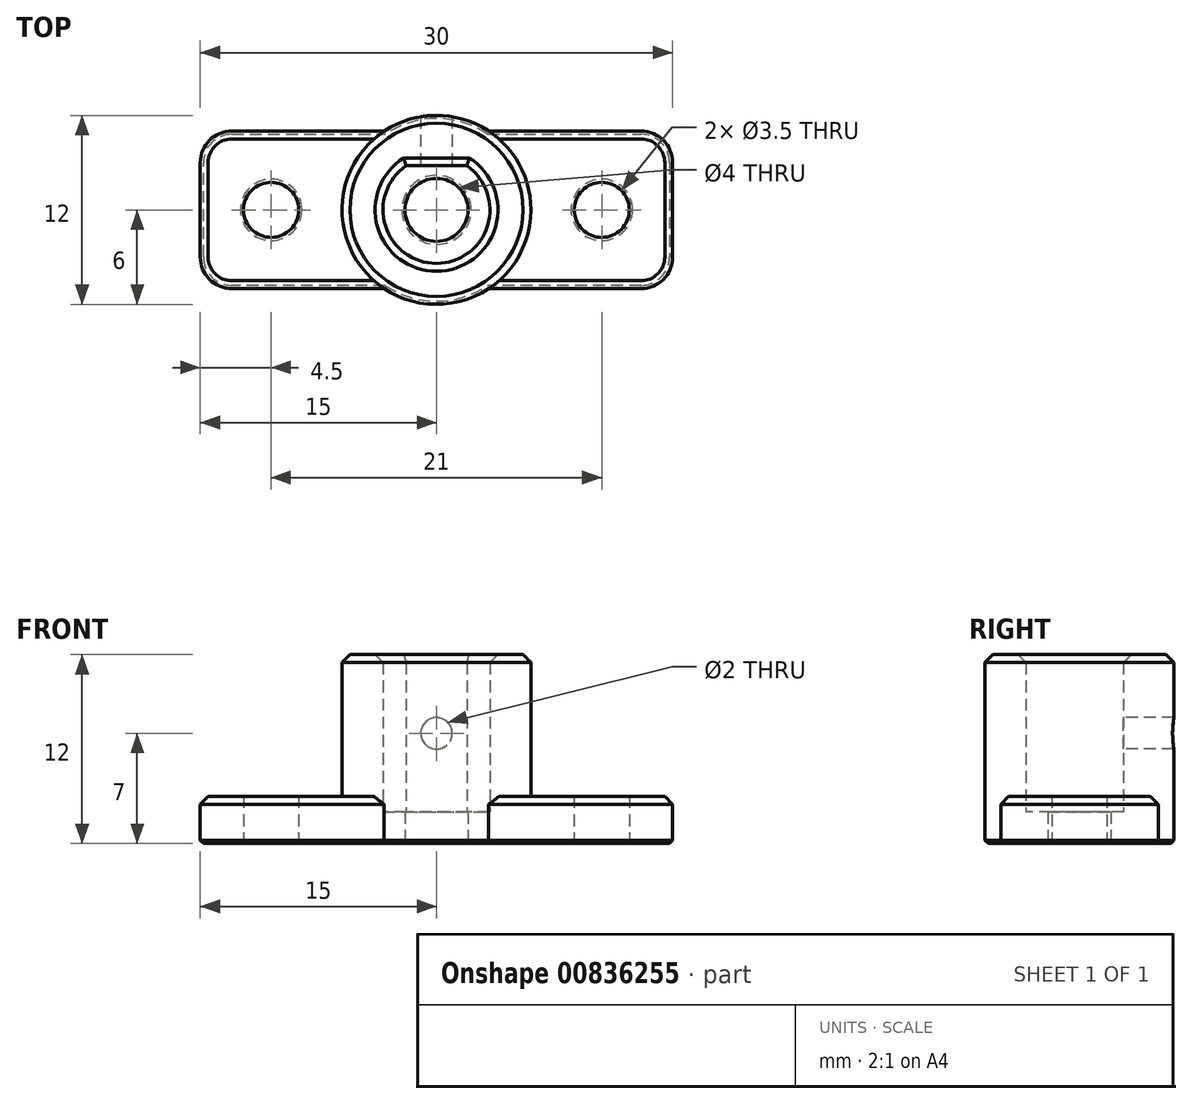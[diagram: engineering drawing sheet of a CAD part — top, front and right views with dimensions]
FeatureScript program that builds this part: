
annotation { "Feature Type Name" : "Feature", "Feature Type Description" : "" }
export const myFeature = defineFeature(function(context is Context, id is Id, definition is map)
    precondition{}
    {
        {
            var Q0;
            Q0=qCreatedBy(makeId("Top.planeOp"),FACE);
            var sketch = newSketch(context, id + "F0", { "sketchPlane" : qUnion([Q0])});
            skArc(sketch, "E0", {"start": v(-1.8, 2.4) * mm, "mid": v(0, -3) * mm, "end": v(1.8, 2.4) * mm, "construction": true});
            skCircle(sketch, "E1", {"center": v(0, 0) * mm, "radius": 6 * mm});
            skLineSegment(sketch, "E2", {"start": v(0, -3) * mm, "end": v(0, 2.4) * mm, "construction": true});
            skLineSegment(sketch, "E3", {"start": v(0, 2.4) * mm, "end": v(1.8, 2.4) * mm, "construction": true});
            skLineSegment(sketch, "E4", {"start": v(0, 2.4) * mm, "end": v(-1.8, 2.4) * mm, "construction": true});
            skLineSegment(sketch, "E5.0", {"start": v(0, 2.8) * mm, "end": v(-1.93, 2.8) * mm});
            skLineSegment(sketch, "E5.1", {"start": v(0, 2.8) * mm, "end": v(1.93, 2.8) * mm});
            skArc(sketch, "E5.2", {"start": v(-1.93, 2.8) * mm, "mid": v(0, -3.4) * mm, "end": v(1.93, 2.8) * mm});
            skLineSegment(sketch, "E6.bottom", {"start": v(13, -5) * mm, "end": v(-13, -5) * mm});
            skLineSegment(sketch, "E6.top", {"start": v(13, 5) * mm, "end": v(-13, 5) * mm});
            skLineSegment(sketch, "E6.left", {"start": v(15, -3) * mm, "end": v(15, 3) * mm});
            skLineSegment(sketch, "E6.right", {"start": v(-15, -3) * mm, "end": v(-15, 3) * mm});
            skLineSegment(sketch, "E7", {"start": v(6, 0) * mm, "end": v(15, 0) * mm, "construction": true});
            skCircle(sketch, "E8", {"center": v(10.5, 0) * mm, "radius": 1.75 * mm});
            skCircle(sketch, "E9.MirrorC", {"center": v(-10.5, 0) * mm, "radius": 1.75 * mm});
            skPoint(sketch, "E10.visualSharp", {"position": v(-15, 5) * mm});
            skArc(sketch, "E10.filletArc", {"start": v(-13, 5) * mm, "mid": v(-14.41, 4.41) * mm, "end": v(-15, 3) * mm});
            skPoint(sketch, "E11.visualSharp", {"position": v(-15, -5) * mm});
            skArc(sketch, "E11.filletArc", {"start": v(-15, -3) * mm, "mid": v(-14.41, -4.41) * mm, "end": v(-13, -5) * mm});
            skPoint(sketch, "E12.visualSharp", {"position": v(15, -5) * mm});
            skArc(sketch, "E12.filletArc", {"start": v(13, -5) * mm, "mid": v(14.41, -4.41) * mm, "end": v(15, -3) * mm});
            skPoint(sketch, "E13.visualSharp", {"position": v(15, 5) * mm});
            skArc(sketch, "E13.filletArc", {"start": v(15, 3) * mm, "mid": v(14.41, 4.41) * mm, "end": v(13, 5) * mm});
            skCircle(sketch, "E14", {"center": v(0, 0) * mm, "radius": 2 * mm});
            skSolve(sketch);
        }
        {
            var Q0;
            Q0=makeQuery(id+"F0.imprint","IMPRINT",FACE,{"disambiguationData":[TD([[makeQuery(id+"F0.imprint","IMPRINT",EDGE,{"derivedFrom":sQuery(id+"F0.wireOp",EDGE,"E5.0")}),-1.0]])]});
            var Q1;
            {var subQ0=sQuery(id+"F0.wireOp",EDGE,"E6.top");var subQ1=sQuery(id+"F0.wireOp",EDGE,"E1");var subQ2=makeQuery(id+"F0.imprint","INTERSECT",VERTEX,{"disambiguationData":[OD(0.0)],"derivedFrom":[subQ1,subQ0]});Q1=makeQuery(id+"F0.imprint","IMPRINT",FACE,{"disambiguationData":[TD([[makeQuery(id+"F0.imprint","IMPRINT",EDGE,{"disambiguationData":[TD([[subQ2,1.0]])],"derivedFrom":subQ1}),1.0]])]});}
            var Q2;
            {var subQ0=sQuery(id+"F0.wireOp",EDGE,"E6.bottom");var subQ1=sQuery(id+"F0.wireOp",EDGE,"E1");var subQ2=makeQuery(id+"F0.imprint","INTERSECT",VERTEX,{"disambiguationData":[OD(0.0)],"derivedFrom":[subQ1,subQ0]});Q2=makeQuery(id+"F0.imprint","IMPRINT",FACE,{"disambiguationData":[TD([[makeQuery(id+"F0.imprint","IMPRINT",EDGE,{"disambiguationData":[TD([[subQ2,-1.0]])],"derivedFrom":subQ1}),1.0]])]});}
            extrude(context, id + "F1", {"entities" : qUnion([Q0, Q1, Q2]), "depth" : 12 * mm, "offsetDistance" : 25 * mm});
        }
        {
            var Q0;
            Q0=makeQuery(id+"F0.imprint","IMPRINT",FACE,{"disambiguationData":[TD([[makeQuery(id+"F0.imprint","IMPRINT",EDGE,{"derivedFrom":sQuery(id+"F0.wireOp",EDGE,"E6.left")}),1.0]])]});
            var Q1;
            Q1=makeQuery(id+"F0.imprint","IMPRINT",FACE,{"disambiguationData":[TD([[makeQuery(id+"F0.imprint","IMPRINT",EDGE,{"derivedFrom":sQuery(id+"F0.wireOp",EDGE,"E6.right")}),-1.0]])]});
            extrude(context, id + "F2", {"entities" : qUnion([Q0, Q1]), "operationType" : NewBodyOperationType.ADD, "depth" : 3 * mm, "offsetDistance" : 25 * mm});
        }
        {
            var Q0;
            Q0=makeQuery(id+"F0.imprint","IMPRINT",FACE,{"disambiguationData":[TD([[makeQuery(id+"F0.imprint","IMPRINT",EDGE,{"derivedFrom":sQuery(id+"F0.wireOp",EDGE,"E5.0")}),1.0]])]});
            extrude(context, id + "F3", {"entities" : qUnion([Q0]), "operationType" : NewBodyOperationType.ADD, "depth" : 2 * mm, "offsetDistance" : 25 * mm});
        }
        {
            var Q0;
            Q0=makeQuery(id+"F1.opExtrude","SWEPT_FACE",FACE,{"disambiguationData":[OSD([sQuery(id+"F0.wireOp",EDGE,"E5.0"),sQuery(id+"F0.wireOp",EDGE,"E5.1")])]});
            var sketch = newSketch(context, id + "F4", { "sketchPlane" : qUnion([Q0])});
            skLineSegment(sketch, "E15", {"start": v(-1.93, 12) * mm, "end": v(1.93, 2) * mm, "construction": true});
            skCircle(sketch, "E16", {"center": v(0, 7) * mm, "radius": 1 * mm});
            skSolve(sketch);
        }
        {
            var Q0;
            Q0=makeQuery(id+"F4.imprint","IMPRINT",FACE,{"disambiguationData":[TD([[makeQuery(id+"F4.imprint","IMPRINT",EDGE,{"derivedFrom":sQuery(id+"F4.wireOp",EDGE,"E16")}),1.0]])]});
            extrude(context, id + "F5", {"entities" : qUnion([Q0]), "operationType" : NewBodyOperationType.REMOVE, "oppositeDirection" : true, "depth" : 25 * mm, "offsetDistance" : 25 * mm});
        }
        {
            var Q0;
            {var subQ0=sQuery(id+"F0.wireOp",EDGE,"E6.bottom");Q0=makeQuery(id+"F2.opExtrude","CAP_EDGE",EDGE,{"disambiguationData":[OSD([subQ0]),TDD([makeQuery(id+"F0.imprint","IMPRINT",EDGE,{"disambiguationData":[TD([[makeQuery(id+"F0.imprint","INTERSECT",VERTEX,{"derivedFrom":[subQ0,sQuery(id+"F0.wireOp",EDGE,"E12.filletArc")]}),-1.0]])],"derivedFrom":subQ0})])],"isStart":false});}
            var Q1;
            Q1=makeQuery(id+"F2.opExtrude","CAP_EDGE",EDGE,{"disambiguationData":[OSD([sQuery(id+"F0.wireOp",EDGE,"E12.filletArc")])],"isStart":false});
            var Q2;
            Q2=makeQuery(id+"F2.opExtrude","CAP_EDGE",EDGE,{"disambiguationData":[OSD([sQuery(id+"F0.wireOp",EDGE,"E6.left")])],"isStart":false});
            var Q3;
            Q3=makeQuery(id+"F2.opExtrude","CAP_EDGE",EDGE,{"disambiguationData":[OSD([sQuery(id+"F0.wireOp",EDGE,"E13.filletArc")])],"isStart":false});
            var Q4;
            {var subQ0=sQuery(id+"F0.wireOp",EDGE,"E6.top");Q4=makeQuery(id+"F2.opExtrude","CAP_EDGE",EDGE,{"disambiguationData":[OSD([subQ0]),TDD([makeQuery(id+"F0.imprint","IMPRINT",EDGE,{"disambiguationData":[TD([[makeQuery(id+"F0.imprint","INTERSECT",VERTEX,{"derivedFrom":[subQ0,sQuery(id+"F0.wireOp",EDGE,"E13.filletArc")]}),-1.0]])],"derivedFrom":subQ0})])],"isStart":false});}
            var Q5;
            {var subQ0=sQuery(id+"F0.wireOp",EDGE,"E6.top");Q5=makeQuery(id+"F2.opExtrude","CAP_EDGE",EDGE,{"disambiguationData":[OSD([subQ0]),TDD([makeQuery(id+"F0.imprint","IMPRINT",EDGE,{"disambiguationData":[TD([[makeQuery(id+"F0.imprint","INTERSECT",VERTEX,{"derivedFrom":[subQ0,sQuery(id+"F0.wireOp",EDGE,"E10.filletArc")]}),1.0]])],"derivedFrom":subQ0})])],"isStart":false});}
            var Q6;
            Q6=makeQuery(id+"F2.opExtrude","CAP_EDGE",EDGE,{"disambiguationData":[OSD([sQuery(id+"F0.wireOp",EDGE,"E10.filletArc")])],"isStart":false});
            var Q7;
            Q7=makeQuery(id+"F2.opExtrude","CAP_EDGE",EDGE,{"disambiguationData":[OSD([sQuery(id+"F0.wireOp",EDGE,"E6.right")])],"isStart":false});
            var Q8;
            Q8=makeQuery(id+"F2.opExtrude","CAP_EDGE",EDGE,{"disambiguationData":[OSD([sQuery(id+"F0.wireOp",EDGE,"E11.filletArc")])],"isStart":false});
            var Q9;
            {var subQ0=sQuery(id+"F0.wireOp",EDGE,"E6.bottom");Q9=makeQuery(id+"F2.opExtrude","CAP_EDGE",EDGE,{"disambiguationData":[OSD([subQ0]),TDD([makeQuery(id+"F0.imprint","IMPRINT",EDGE,{"disambiguationData":[TD([[makeQuery(id+"F0.imprint","INTERSECT",VERTEX,{"derivedFrom":[subQ0,sQuery(id+"F0.wireOp",EDGE,"E11.filletArc")]}),1.0]])],"derivedFrom":subQ0})])],"isStart":false});}
            var Q10;
            Q10=makeQuery(id+"F1.opExtrude","CAP_EDGE",EDGE,{"disambiguationData":[OSD([sQuery(id+"F0.wireOp",EDGE,"E1")])],"isStart":false});
            var Q11;
            Q11=makeQuery(id+"F1.opExtrude","CAP_EDGE",EDGE,{"disambiguationData":[OSD([sQuery(id+"F0.wireOp",EDGE,"E5.2")])],"isStart":false});
            var Q12;
            Q12=makeQuery(id+"F1.opExtrude","CAP_EDGE",EDGE,{"disambiguationData":[OSD([sQuery(id+"F0.wireOp",EDGE,"E5.0"),sQuery(id+"F0.wireOp",EDGE,"E5.1")])],"isStart":false});
            chamfer(context, id + "F6", {"entities" : qUnion([Q0, Q1, Q2, Q3, Q4, Q5, Q6, Q7, Q8, Q9, Q10, Q11, Q12]), "width" : 0.5 * mm, "tangentPropagation" : true});
        }
        {
            var Q0;
            {var subQ0=sQuery(id+"F0.wireOp",EDGE,"E6.top");Q0=makeQuery(id+"F2.opExtrude","CAP_EDGE",EDGE,{"disambiguationData":[OSD([subQ0]),TDD([makeQuery(id+"F0.imprint","IMPRINT",EDGE,{"disambiguationData":[TD([[makeQuery(id+"F0.imprint","INTERSECT",VERTEX,{"derivedFrom":[subQ0,sQuery(id+"F0.wireOp",EDGE,"E13.filletArc")]}),-1.0]])],"derivedFrom":subQ0})])],"isStart":true});}
            var Q1;
            {var subQ1=sQuery(id+"F0.wireOp",EDGE,"E6.top");var subQ3=sQuery(id+"F0.wireOp",EDGE,"E1");var subQ4=sQuery(id+"F0.wireOp",EDGE,"E13.filletArc");Q1=makeQuery(id+"F2.boolean.opBoolean","SPLIT",EDGE,{"disambiguationData":[TD([makeQuery(id+"F2.opExtrude","SWEPT_FACE",FACE,{"disambiguationData":[OSD([subQ1]),TDD([makeQuery(id+"F0.imprint","IMPRINT",EDGE,{"disambiguationData":[TD([[makeQuery(id+"F0.imprint","INTERSECT",VERTEX,{"derivedFrom":[subQ1,subQ4]}),-1.0]])],"derivedFrom":subQ1})])]})])],"derivedFrom":makeQuery(id+"F1.opExtrude","CAP_EDGE",EDGE,{"disambiguationData":[OSD([subQ3])],"isStart":true})});}
            var Q2;
            {var subQ2=sQuery(id+"F0.wireOp",EDGE,"E6.bottom");var subQ3=sQuery(id+"F0.wireOp",EDGE,"E1");var subQ4=sQuery(id+"F0.wireOp",EDGE,"E12.filletArc");Q2=makeQuery(id+"F2.boolean.opBoolean","SPLIT",EDGE,{"disambiguationData":[TD([makeQuery(id+"F2.opExtrude","SWEPT_FACE",FACE,{"disambiguationData":[OSD([subQ2]),TDD([makeQuery(id+"F0.imprint","IMPRINT",EDGE,{"disambiguationData":[TD([[makeQuery(id+"F0.imprint","INTERSECT",VERTEX,{"derivedFrom":[subQ2,subQ4]}),-1.0]])],"derivedFrom":subQ2})])]})])],"derivedFrom":makeQuery(id+"F1.opExtrude","CAP_EDGE",EDGE,{"disambiguationData":[OSD([subQ3])],"isStart":true})});}
            var Q3;
            {var subQ0=sQuery(id+"F0.wireOp",EDGE,"E6.bottom");Q3=makeQuery(id+"F2.opExtrude","CAP_EDGE",EDGE,{"disambiguationData":[OSD([subQ0]),TDD([makeQuery(id+"F0.imprint","IMPRINT",EDGE,{"disambiguationData":[TD([[makeQuery(id+"F0.imprint","INTERSECT",VERTEX,{"derivedFrom":[subQ0,sQuery(id+"F0.wireOp",EDGE,"E11.filletArc")]}),1.0]])],"derivedFrom":subQ0})])],"isStart":true});}
            var Q4;
            Q4=makeQuery(id+"F2.opExtrude","CAP_EDGE",EDGE,{"disambiguationData":[OSD([sQuery(id+"F0.wireOp",EDGE,"E8")])],"isStart":true});
            var Q5;
            Q5=makeQuery(id+"F3.opExtrude","CAP_EDGE",EDGE,{"disambiguationData":[OSD([sQuery(id+"F0.wireOp",EDGE,"E14")])],"isStart":true});
            var Q6;
            Q6=makeQuery(id+"F2.opExtrude","CAP_EDGE",EDGE,{"disambiguationData":[OSD([sQuery(id+"F0.wireOp",EDGE,"E9.MirrorC")])],"isStart":true});
            chamfer(context, id + "F7", {"entities" : qUnion([Q0, Q1, Q2, Q3, Q4, Q5, Q6]), "width" : 0.2 * mm, "tangentPropagation" : true});
        }
    });
